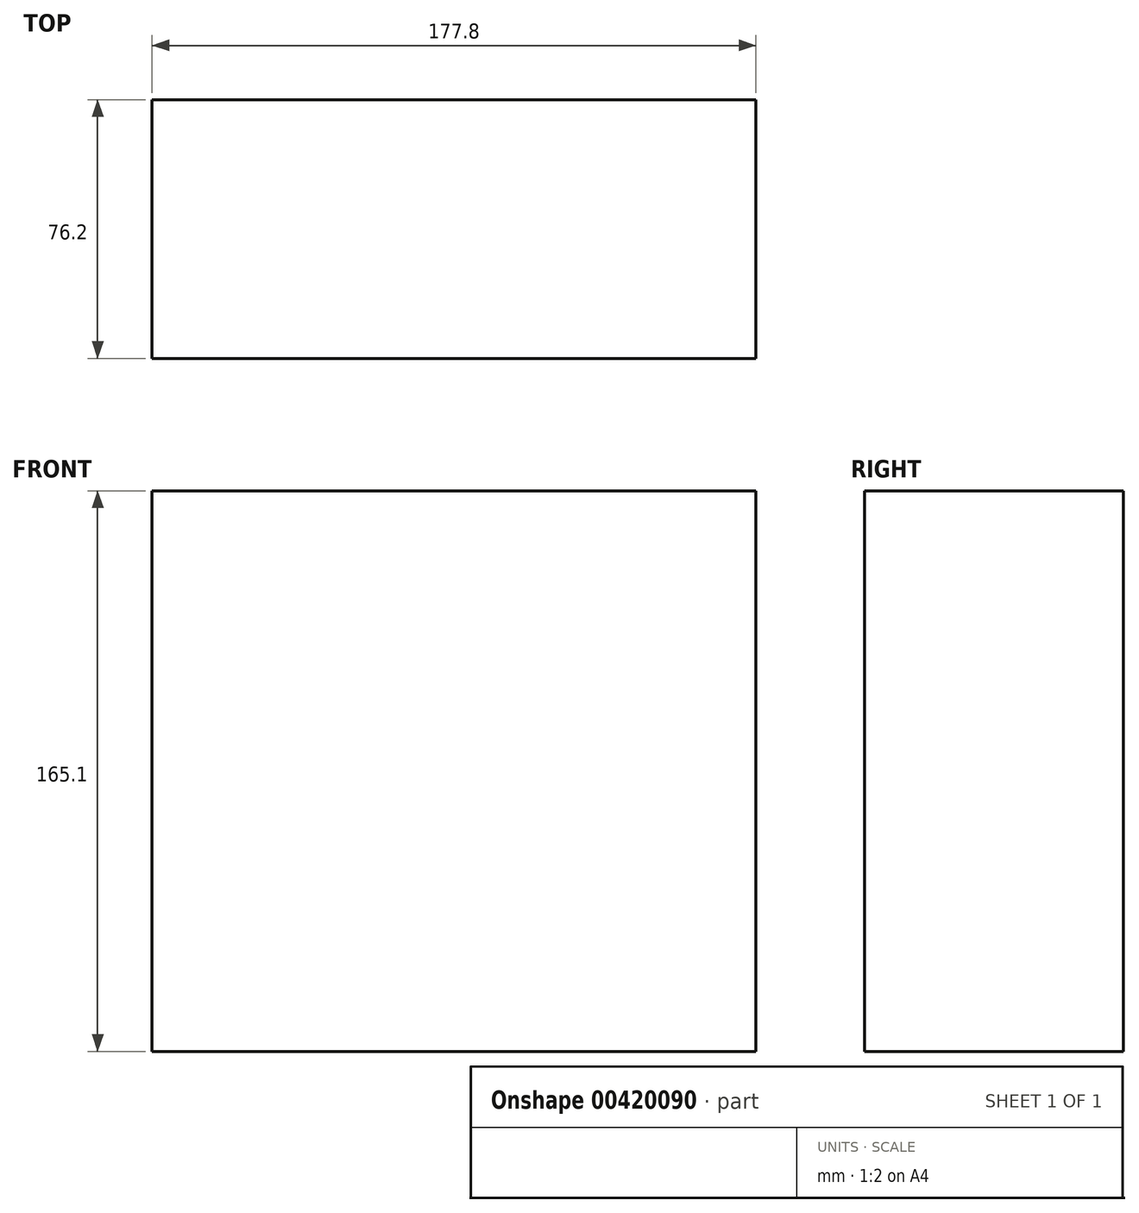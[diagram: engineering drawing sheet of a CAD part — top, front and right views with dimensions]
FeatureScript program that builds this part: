
annotation { "Feature Type Name" : "Feature", "Feature Type Description" : "" }
export const myFeature = defineFeature(function(context is Context, id is Id, definition is map)
    precondition{}
    {
        {
            var Q0;
            Q0=qCreatedBy(makeId("Front.planeOp"),FACE);
            var sketch = newSketch(context, id + "F0", { "sketchPlane" : qUnion([Q0])});
            skLineSegment(sketch, "E0.bottom", {"start": v(-93.79, 134.16) * mm, "end": v(84.01, 134.16) * mm});
            skLineSegment(sketch, "E0.top", {"start": v(-93.79, -30.94) * mm, "end": v(84.01, -30.94) * mm});
            skLineSegment(sketch, "E0.left", {"start": v(-93.79, 134.16) * mm, "end": v(-93.79, -30.94) * mm});
            skLineSegment(sketch, "E0.right", {"start": v(84.01, 134.16) * mm, "end": v(84.01, -30.94) * mm});
            skSolve(sketch);
        }
        {
            var Q0;
            Q0=makeQuery(id+"F0.imprint","IMPRINT",FACE,{"disambiguationData":[TD([[makeQuery(id+"F0.imprint","IMPRINT",EDGE,{"derivedFrom":sQuery(id+"F0.wireOp",EDGE,"E0.bottom")}),-1.0]])]});
            extrude(context, id + "F1", {"entities" : qUnion([Q0]), "depth" : 76.2 * mm});
        }
    });
